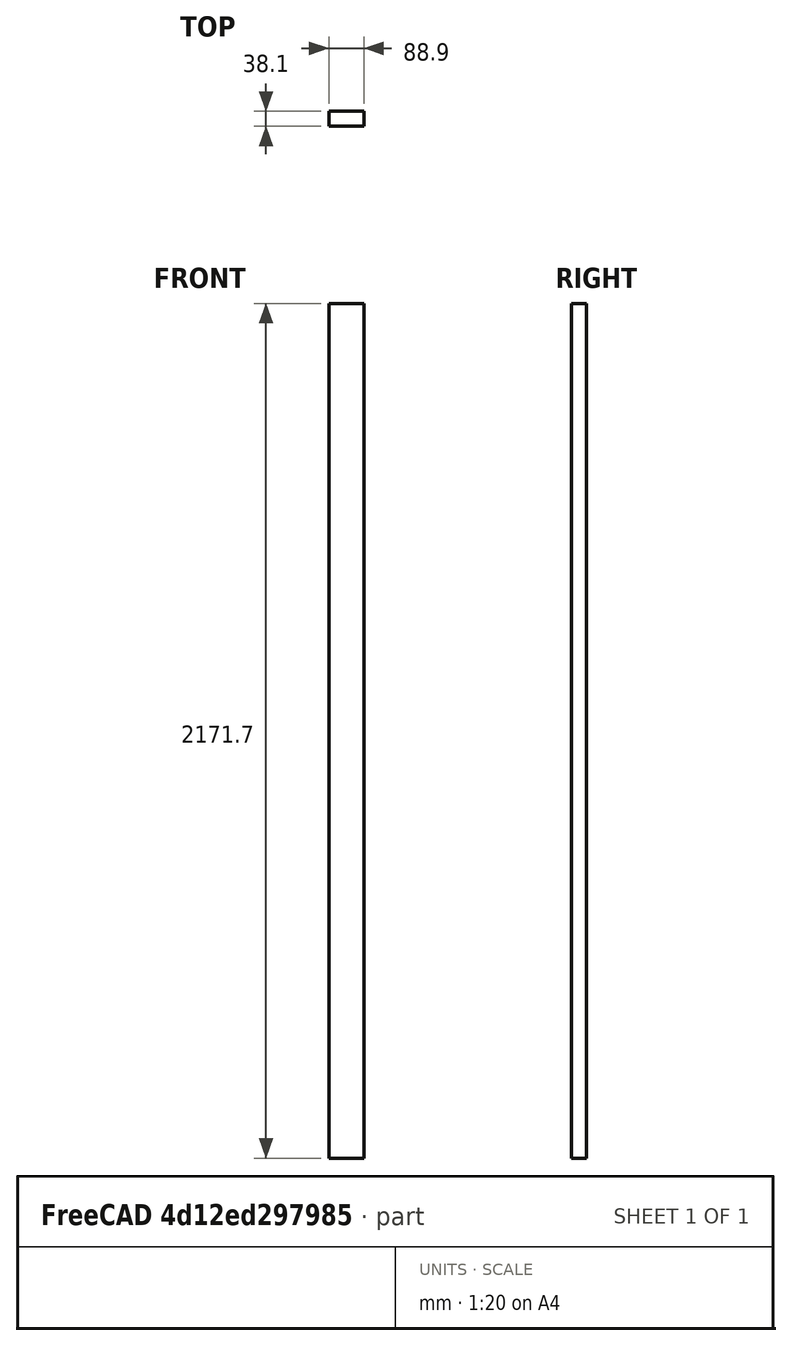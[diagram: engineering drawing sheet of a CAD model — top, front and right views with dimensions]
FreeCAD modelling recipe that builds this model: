
FCSTD DOCUMENT  (FreeCAD 2023.131R26244 +5365 (Git))
Label: verticalTimber
License: All rights reserved
LicenseURL: http://en.wikipedia.org/wiki/All_rights_reserved
objects: Sketcher::SketchObject×1, PartDesign::Pad×1, PartDesign::Body×1, App::Part×1
note: 6 computed .brp shape members not serialized (recipe doc carries the construction recipe); baked Part::Feature solids carry a one-line shape summary decoded from their .brp

FEATURE [Sketcher::SketchObject] Sketch
  ArcFitTolerance = 1e-06
  AttachmentSupport = -> [XY_Plane]
  ExternalBSplineMaxDegree = 5
  ExternalBSplineTolerance = 0.0001
  FixShape = 1
  FullyConstrained = true
  InternalTolerance = 1e-06
  InvalidShape = false
  MakeInternals = false
  MapMode = 5
  Support = -> [XY_Plane]
  TreeRank = 13
  ValidateShape = false
  sketch-geometry (4):
    g0: LineSegment StartX=0 StartY=0 StartZ=0 EndX=88.9 EndY=0 EndZ=0
    g1: LineSegment StartX=88.9 StartY=0 StartZ=0 EndX=88.9 EndY=38.1 EndZ=0
    g2: LineSegment StartX=88.9 StartY=38.1 StartZ=0 EndX=0 EndY=38.1 EndZ=0
    g3: LineSegment StartX=0 StartY=38.1 StartZ=0 EndX=0 EndY=0 EndZ=0
  constraints (11):
    c: Coincident(g0,g1)
    c: Coincident(g1,g2)
    c: Coincident(g2,g3)
    c: Coincident(g3,g0)
    c: Horizontal(g0)
    c: Horizontal(g2)
    c: Vertical(g1)
    c: Vertical(g3)
    c: Coincident(g0,g-1)
    c: DistanceX(g0,g0) = 88.9
    c: DistanceY(g3,g3) = 38.1
FEATURE [PartDesign::Pad] Pad
  AddSubType = 0
  AlongSketchNormal = false
  AutoTaperInnerAngle = true
  CheckUpToFaceLimits = true
  ClaimChildren = false
  Direction = (0,0,1)
  Fit = 0
  FitJoin = 0
  FixShape = 1
  InnerFit = 0
  InnerFitJoin = 0
  InvalidShape = false
  Length = 2171.7
  Length2 = 100
  Linearize = true
  NewSolid = false
  Profile = -> Sketch
  Suppress = false
  TaperInnerAngle = 0
  TaperInnerAngleRev = 0
  TreeRank = 14
  Type = 0
  ValidateShape = false
  _ProfileBasedVersion = 1
FEATURE [PartDesign::Body] Body
  AutoGroupSolids = false
  ClaimAllChildren = false
  ExportMode = 0
  FixShape = 1
  Group = -> [Sketch,Pad]
  InvalidShape = false
  Origin = -> Origin001
  Tip = -> Pad
  TreeRank = 12
  ValidateShape = false
  _ExportChildren = -> [Pad]
  _GroupVersion = 1
FEATURE [App::Part] Part  label="verticalTimber-Part"
  ClaimAllChildren = false
  ExportMode = 1
  Group = -> [Body]
  Origin = -> Origin
  TreeRank = 1
  _ExportChildren = -> [Body]
  _GroupVersion = 1
